# Revit family: Damper-Control-Carnes-Round-FAHA
name_source: partatom
category: Duct Accessories
revit_build: Autodesk Revit MEP 2012 (Build: 20110309_2315(x64)
units: mm (PartAtom-declared; Revit-internal decimal feet)

## types (43) — shared parameters
04 CSI = 08 91 00
95 CSI = 10200
Assembly Code = D3090700
Bearing Lenght = 4 "
Blade Material = Aluminum - Carnes - Extruded
Catalog URL = http://www.carnes.com
Connector Descriptor 1 = Duct Connection 1
Connector Descriptor 2 = Duct Connection 2
Damper Air Flow = 0 CFM
Depth = 8 "
Description = Round Dampers
Frame Material = Aluminum - Carnes - Extruded
Manufacturer = Carnes Company
Manufacturer Fax = 608-845-6470
Maximum Horinzontal Size = 46" Diameter
Maximum Vertical Size = 46" Diameter
Minimum Size = 4" Diameter
Model = FAHA
Pressure Drop = 0.00 in-wg
Product Line = Round Dampers
Product Page URL = http://www.carnes.com
Specifications URL = http://www.carnes.com
Subcategory = Louvers and Dampers
URL = http://www.carnes.com
ecoScorecard Product Page = http://www.ecoscorecard.com

## per-type parameters (varying)
| type | Body and Blade Gauge | Diameter | Diameter Control | Duct Connection Radius | Maximum Pressure Differential | Maximum Velocity | Outside Diameter | Shaft Diameter |
| 4” Dia - 2600 Max Velocity | 24 ga. | 4 " | 4 " | 2 " | 6 " | 2600 FPM | 4.13 " | 0.5 " |
| 5” Dia - 2600 Max Velocity | 24 ga. | 5 " | 5 " | 2.5 " | 6 " | 2600 FPM | 5.13 " | 0.5 " |
| 6” Dia - 2600 Max Velocity | 24 ga. | 6 " | 6 " | 3 " | 6 " | 2600 FPM | 6.13 " | 0.5 " |
| 7” Dia - 2600 Max Velocity | 24 ga. | 7 " | 7 " | 3.5 " | 6 " | 2600 FPM | 7.13 " | 0.5 " |
| 8” Dia - 2600 Max Velocity | 24 ga. | 8 " | 8 " | 4 " | 6 " | 2600 FPM | 8.13 " | 0.5 " |
| 9” Dia - 2600 Max Velocity | 24 ga. | 9 " | 9 " | 4.5 " | 6 " | 2600 FPM | 9.13 " | 0.5 " |
| 10” Dia - 2400 Max Velocity | 24 ga. | 10 " | 10 " | 5 " | 5 " | 2400 FPM | 10.13 " | 0.5 " |
| 11” Dia - 2400 Max Velocity | 24 ga. | 11 " | 11 " | 5.5 " | 5 " | 2400 FPM | 11.13 " | 0.5 " |
| 12” Dia - 2400 Max Velocity | 20 ga. | 12 " | 12 " | 6 " | 5 " | 2400 FPM | 12.13 " | 0.5 " |
| 13” Dia - 2400 Max Velocity | 20 ga. | 13 " | 13 " | 6.5 " | 5 " | 2400 FPM | 13.13 " | 0.5 " |
| 14” Dia - 2300 Max Velocity | 20 ga. | 14 " | 14 " | 7 " | 4 " | 2300 FPM | 14.13 " | 0.5 " |
| 15” Dia - 2300 Max Velocity | 20 ga. | 15 " | 15 " | 7.5 " | 4 " | 2300 FPM | 15.13 " | 0.5 " |
| 16” Dia - 2300 Max Velocity | 20 ga. | 16 " | 16 " | 8 " | 4 " | 2300 FPM | 16.13 " | 0.5 " |
| 17” Dia - 2300 Max Velocity | 20 ga. | 17 " | 17 " | 8.5 " | 4 " | 2300 FPM | 17.13 " | 0.5 " |
| 18” Dia - 2300 Max Velocity | 20 ga. | 18 " | 18 " | 9 " | 4 " | 2300 FPM | 18.13 " | 0.5 " |
| 19” Dia - 2300 Max Velocity | 20 ga. | 19 " | 19 " | 9.5 " | 4 " | 2300 FPM | 19.13 " | 0.5 " |
| 20” Dia - 2300 Max Velocity | 20 ga. | 20 " | 20 " | 10 " | 4 " | 2300 FPM | 20.13 " | 0.5 " |
| 21” Dia - 2300 Max Velocity | 20 ga. | 21 " | 21 " | 10.5 " | 4 " | 2300 FPM | 21.13 " | 0.5 " |
| 22” Dia - 2300 Max Velocity | 20 ga. | 22 " | 22 " | 11 " | 4 " | 2300 FPM | 22.13 " | 0.5 " |
| 23” Dia - 2300 Max Velocity | 20 ga. | 23 " | 23 " | 11.5 " | 4 " | 2300 FPM | 23.13 " | 0.5 " |
| 24” Dia - 2300 Max Velocity | 20 ga. | 24 " | 24 " | 12 " | 4 " | 2300 FPM | 24.13 " | 0.5 " |
| 25” Dia - 2300 Max Velocity | 20 ga. | 25 " | 25 " | 12.5 " | 4 " | 2300 FPM | 25.13 " | 0.5 " |
| 26” Dia - 2200 Max Velocity | 20 ga. | 26 " | 26 " | 13 " | 2.5 " | 2200 FPM | 26.13 " | 0.5 " |
| 27” Dia - 2200 Max Velocity | 20 ga. | 27 " | 27 " | 13.5 " | 2.5 " | 2200 FPM | 27.13 " | 0.5 " |
| 28” Dia - 2200 Max Velocity | 20 ga. | 28 " | 28 " | 14 " | 2.5 " | 2200 FPM | 28.13 " | 0.5 " |
| 29” Dia - 2200 Max Velocity | 20 ga. | 29 " | 29 " | 14.5 " | 2.5 " | 2200 FPM | 29.13 " | 0.5 " |
| 30” Dia - 2200 Max Velocity | 20 ga. | 30 " | 30 " | 15 " | 2.5 " | 2200 FPM | 30.13 " | 0.5 " |
| 31” Dia - 2200 Max Velocity | 20 ga. | 31 " | 31 " | 15.5 " | 2.5 " | 2200 FPM | 31.13 " | 0.5 " |
| 32” Dia - 2000 Max Velocity | 18" | 32 " | 32 " | 16 " | 1.75 " | 2000 FPM | 32.13 " | 0.75 " |
| 33” Dia - 2000 Max Velocity | 18" | 33 " | 33 " | 16.5 " | 1.75 " | 2000 FPM | 33.13 " | 0.75 " |
| 34” Dia - 2000 Max Velocity | 18" | 34 " | 34 " | 17 " | 1.75 " | 2000 FPM | 34.13 " | 0.75 " |
| 35” Dia - 2000 Max Velocity | 18" | 35 " | 35 " | 17.5 " | 1.75 " | 2000 FPM | 35.13 " | 0.75 " |
| 36” Dia - 2000 Max Velocity | 18" | 36 " | 36 " | 18 " | 1.75 " | 2000 FPM | 36.13 " | 0.75 " |
| 37” Dia - 2000 Max Velocity | 18" | 37 " | 37 " | 18.5 " | 1.75 " | 2000 FPM | 37.13 " | 0.75 " |
| 38” Dia - 2000 Max Velocity | 18" | 38 " | 38 " | 19 " | 1.75 " | 2000 FPM | 38.13 " | 0.75 " |
| 39” Dia - 2000 Max Velocity | 18" | 39 " | 39 " | 19.5 " | 1.75 " | 2000 FPM | 39.13 " | 0.75 " |
| 40” Dia - 2000 Max Velocity | 18" | 40 " | 40 " | 20 " | 1.75 " | 2000 FPM | 40.13 " | 0.75 " |
| 41” Dia - 2000 Max Velocity | 18" | 41 " | 41 " | 20.5 " | 1.75 " | 2000 FPM | 41.13 " | 0.75 " |
| 42” Dia - 2000 Max Velocity | 18" | 42 " | 42 " | 21 " | 1.75 " | 2000 FPM | 42.13 " | 0.75 " |
| 43” Dia - 2000 Max Velocity | 18" | 43 " | 43 " | 21.5 " | 1.75 " | 2000 FPM | 43.13 " | 0.75 " |
| 44” Dia - 2000 Max Velocity | 18" | 44 " | 44 " | 22 " | 1.75 " | 2000 FPM | 44.13 " | 0.75 " |
| 45” Dia - 2000 Max Velocity | 18" | 45 " | 45 " | 22.5 " | 1.75 " | 2000 FPM | 45.13 " | 0.75 " |
| 46” Dia - 2000 Max Velocity | 18" | 46 " | 46 " | 23 " | 1.75 " | 2000 FPM | 46.13 " | 0.75 " |

## geometry (parser evidence)
native form markers: Sweep x1
no freeform markers — native parametric forms only
